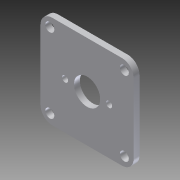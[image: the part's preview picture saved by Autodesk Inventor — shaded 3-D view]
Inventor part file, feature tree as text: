
AUTODESK INVENTOR PART (.ipt)
format: ipt  version: 2012 (Build 160160000, 160)  size: 145,408 bytes
history: native  units: in
note: dims shown in document units (in); Inventor stores cm internally (conversion verified against a paired STEP export)
features: extrude x2, hole x2, sketch x1, fillet x1
ambient origin geometry x8: Origin, YZ Plane, XZ Plane, XY Plane, X Axis, Y Axis, Z Axis, Center Point
bodies: Solid1 (feature_tree)
feature tree (6):
  sketch  "Sketch1"  dims[d0=0.9449in d1=0.4724in d2=1.0236in d3=0.5118in d4=0.0787in d5=0.2559in d6=0.128in d7=0.0787in d8=0.5625in d9=2.0in d10=1.0in d11=2.0in d12=1.0in d13=0.1181in d14=0.3937in d15=0.1575in d16=0.1575in d17=0.1575in d18=0.1575in d19=0.1575in d20=0.2in d21=0.2in d22=0.2in d23=0.2in d24=0.125in d25=0.0in d34=1.6in d35=1.6in d44=0.25in d53=0.1935in d54=0.75in d55=0.375in d56=0.25in d57=0.5635in d58=1.0in d59=0.8108in d61=0.4724in d62=0.4724in d63=1.0in d64=0.0in d65=0.131in d66=0.75in d67=0.375in d68=0.25in d69=0.5635in d70=1.0in d71=0.8108in]
  extrude  "Extrusion1"  Depth=0.4724in
  fillet  "Fillet2"  Radius=1.0236in
  hole  "Hole2"  [1 undecoded]
  extrude  "Extrusion6"  Depth=0.0787in
  hole  "Hole3"  [1 undecoded]
note: 2 required parameter values undecoded (feature->parameter linkage not recoverable at this tier; creation-order binding heuristic only, values carry confidence <= 0.55)
